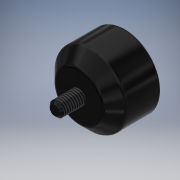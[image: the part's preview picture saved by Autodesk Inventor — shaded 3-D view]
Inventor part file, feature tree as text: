
AUTODESK INVENTOR PART (.ipt)
format: ipt  version: 2019 (Build 230136000, 136)  size: 173,568 bytes
history: native  units: mm
features: extrude x5, sketch x5, fillet x3, plane x3, chamfer x2, thread x1
ambient origin geometry x8: Origin, YZ Plane, XZ Plane, XY Plane, X Axis, Y Axis, Z Axis, Center Point
bodies: Solid1 (feature_tree)
feature tree (19):
  extrude  "Extrusion1"  Depth=20.0mm TaperAngle=0.0deg
  extrude  "Extrusion3"  Depth=2.0mm TaperAngle=45.0deg
  chamfer  "Chamfer1"  Distance=10.0mm
  fillet  "Fillet1"  Radius=1.0mm
  extrude  "Extrusion4"  Depth=1.0mm
  chamfer  "Chamfer2"  Distance=15.0mm
  fillet  "Fillet2"  Radius=12.0mm
  plane  "Work Plane2"
  plane  "Work Plane3"
  extrude  "Extrusion5"  Depth=1.0mm
  thread  "Thread1"  [1 undecoded]
  extrude  "Extrusion6"  Depth=1.0mm
  fillet  "Fillet3"  [1 undecoded]
  sketch  "Sketch1"  dims[d0=30.0mm d1=20.0mm d2=0.0mm]
  sketch  "Sketch3"  dims[d6=1.0mm d7=0.0mm d8=5.0mm d9=2.0mm d10=45.0deg]
  sketch  "Sketch4"  dims[d11=2.0mm]
  plane  "Work Plane1"
  sketch  "Sketch5"  dims[d12=6.0mm d13=10.0mm d14=0.0mm]
  sketch  "Sketch6"  dims[d15=1.0mm d16=2.0mm d17=45.0deg d18=1.0mm d19=-15.5mm d20=30.0mm d27=-14.75mm d28=15.0mm d29=12.0mm d30=7.5mm d31=7.5mm d32=1.5mm d34=0.0mm d36=20.0mm d37=0.0mm d38=5.0mm d39=0.0mm d40=10.0mm d41=0.0mm d42=10.0mm d43=0.0mm d44=1.0mm]
note: 2 required parameter values undecoded (feature->parameter linkage not recoverable at this tier; creation-order binding heuristic only, values carry confidence <= 0.55)
